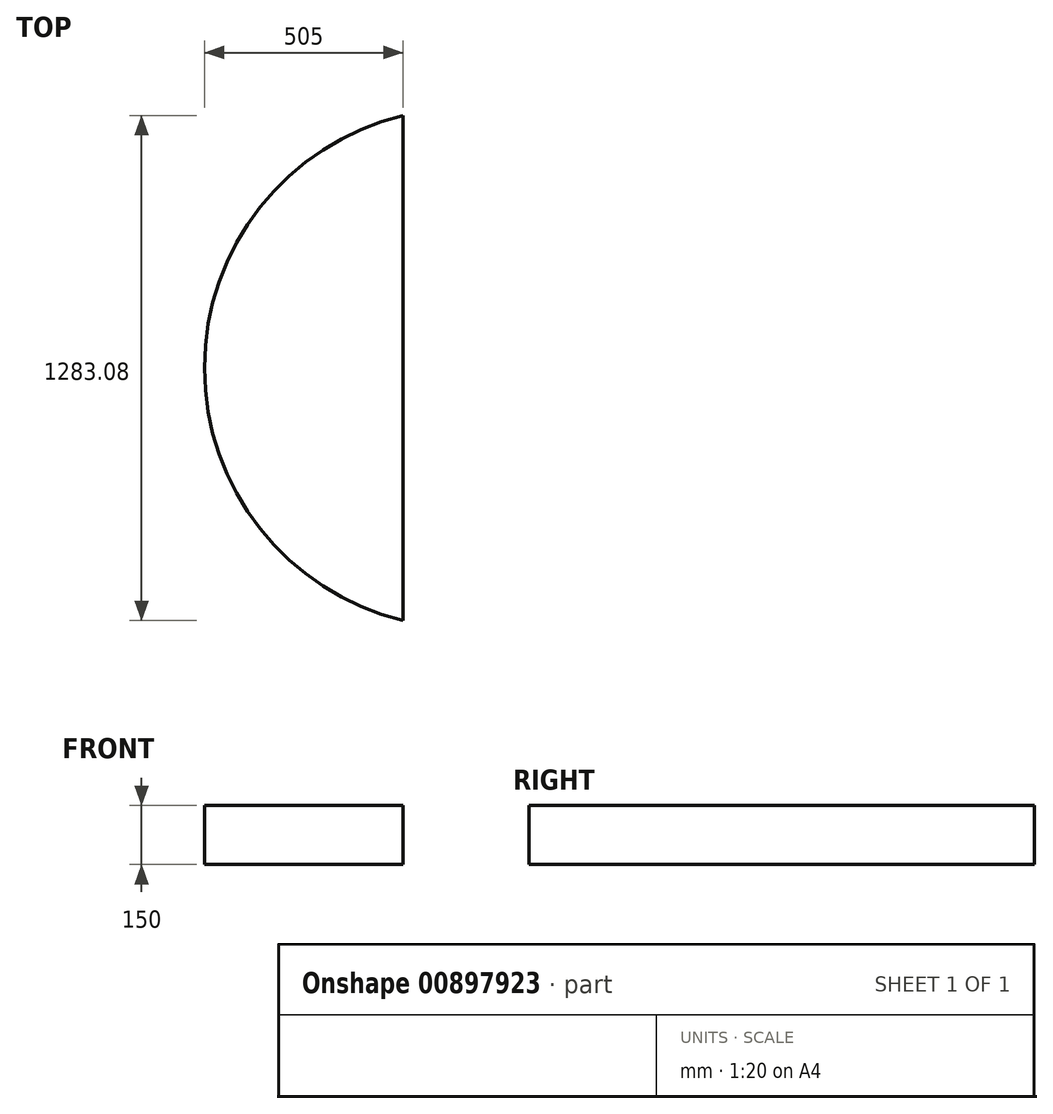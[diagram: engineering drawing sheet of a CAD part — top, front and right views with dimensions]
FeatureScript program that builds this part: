
annotation { "Feature Type Name" : "Feature", "Feature Type Description" : "" }
export const myFeature = defineFeature(function(context is Context, id is Id, definition is map)
    precondition{}
    {
        {
            var Q0;
            Q0=qCreatedBy(makeId("Top.planeOp"),FACE);
            var sketch = newSketch(context, id + "F0", { "sketchPlane" : qUnion([Q0])});
            skCircle(sketch, "E0", {"center": v(0, 0) * mm, "radius": 660 * mm});
            skLineSegment(sketch, "E1", {"start": v(155, 641.54) * mm, "end": v(155, -641.54) * mm});
            skLineSegment(sketch, "E2", {"start": v(-155, 641.54) * mm, "end": v(-155, -641.54) * mm});
            skLineSegment(sketch, "E3", {"start": v(155, 0) * mm, "end": v(-155, 0) * mm, "construction": true});
            skSolve(sketch);
        }
        {
            var Q0;
            {var subQ0=sQuery(id+"F0.wireOp",EDGE,"E2");Q0=makeQuery(id+"F0.imprint","IMPRINT",FACE,{"disambiguationData":[TD([[makeQuery(id+"F0.imprint","IMPRINT",EDGE,{"derivedFrom":subQ0}),-1.0]])]});}
            extrude(context, id + "F1", {"entities" : qUnion([Q0]), "endBound" : BoundingType.SYMMETRIC, "depth" : 150 * mm, "offsetDistance" : 25 * mm});
        }
    });
